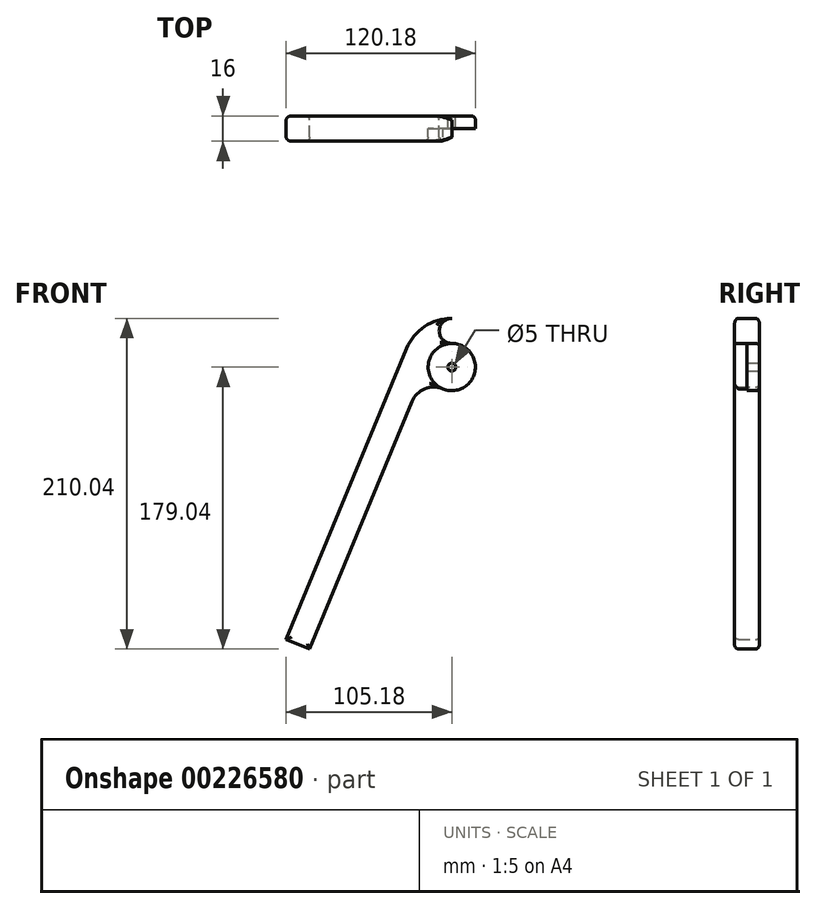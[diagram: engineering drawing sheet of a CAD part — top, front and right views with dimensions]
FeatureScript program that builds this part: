
annotation { "Feature Type Name" : "Feature", "Feature Type Description" : "" }
export const myFeature = defineFeature(function(context is Context, id is Id, definition is map)
    precondition{}
    {
        {
            var Q0;
            Q0=qCreatedBy(makeId("Front.planeOp"),FACE);
            var sketch = newSketch(context, id + "F0", { "sketchPlane" : qUnion([Q0])});
            skCircle(sketch, "E0", {"center": v(0, 0) * mm, "radius": 15 * mm});
            skCircle(sketch, "E1", {"center": v(0, 23) * mm, "radius": 8 * mm});
            skLineSegment(sketch, "E2", {"start": v(0, 0) * mm, "end": v(-46.2, 19.13) * mm});
            skArc(sketch, "E3", {"start": v(0, 31) * mm, "mid": v(-17.22, 25.78) * mm, "end": v(-28.64, 11.86) * mm});
            skLineSegment(sketch, "E4", {"start": v(-28.64, 11.86) * mm, "end": v(-105.18, -172.91) * mm});
            skLineSegment(sketch, "E5", {"start": v(-105.18, -172.91) * mm, "end": v(-90.4, -179.04) * mm});
            skLineSegment(sketch, "E6", {"start": v(-90.4, -179.04) * mm, "end": v(-13.86, 5.74) * mm});
            skLineSegment(sketch, "E7", {"start": v(0, 0) * mm, "end": v(-21.14, -51.03) * mm});
            skArc(sketch, "E8", {"start": v(-5.74, -13.86) * mm, "mid": v(-17.22, -13.86) * mm, "end": v(-25.34, -21.98) * mm});
            skSolve(sketch);
        }
        {
            var Q0;
            {var subQ3=sQuery(id+"F0.wireOp",EDGE,"E4");Q0=makeQuery(id+"F0.imprint","IMPRINT",FACE,{"disambiguationData":[TD([[makeQuery(id+"F0.imprint","IMPRINT",EDGE,{"derivedFrom":subQ3}),1.0]])]});}
            var Q1;
            {var subQ5=sQuery(id+"F0.wireOp",EDGE,"E3");Q1=makeQuery(id+"F0.imprint","IMPRINT",FACE,{"disambiguationData":[TD([[makeQuery(id+"F0.imprint","IMPRINT",EDGE,{"derivedFrom":subQ5}),1.0]])]});}
            var Q2;
            {var subQ3=sQuery(id+"F0.wireOp",EDGE,"E8");Q2=makeQuery(id+"F0.imprint","IMPRINT",FACE,{"disambiguationData":[TD([[makeQuery(id+"F0.imprint","IMPRINT",EDGE,{"derivedFrom":subQ3}),-1.0]])]});}
            extrude(context, id + "F1", {"entities" : qUnion([Q0, Q1, Q2]), "depth" : 16 * mm});
        }
        {
            var Q0;
            {var subQ0=sQuery(id+"F0.wireOp",EDGE,"E2");var subQ3=sQuery(id+"F0.wireOp",EDGE,"E7");var subQ5=makeQuery(id+"F0.imprint","INTERSECT",VERTEX,{"derivedFrom":[subQ0,subQ3]});Q0=makeQuery(id+"F0.imprint","IMPRINT",FACE,{"disambiguationData":[TD([[makeQuery(id+"F0.imprint","IMPRINT",EDGE,{"disambiguationData":[TD([[subQ5,-1.0]])],"derivedFrom":subQ0}),1.0]])]});}
            var Q1;
            {var subQ1=sQuery(id+"F0.wireOp",EDGE,"E0");var subQ3=makeQuery(id+"F0.imprint","INTERSECT",VERTEX,{"derivedFrom":[subQ1,sQuery(id+"F0.wireOp",EDGE,"E1")]});Q1=makeQuery(id+"F0.imprint","IMPRINT",FACE,{"disambiguationData":[TD([[makeQuery(id+"F0.imprint","IMPRINT",EDGE,{"disambiguationData":[TD([[subQ3,-1.0]])],"derivedFrom":subQ1}),1.0]])]});}
            extrude(context, id + "F2", {"entities" : qUnion([Q0, Q1]), "operationType" : NewBodyOperationType.ADD, "depth" : 8 * mm});
        }
        {
            var Q0;
            Q0=makeQuery(id+"F1.opExtrude","CAP_FACE",FACE,{"disambiguationData":[OSD([sQuery(id+"F0.wireOp",EDGE,"E0"),sQuery(id+"F0.wireOp",EDGE,"E1"),sQuery(id+"F0.wireOp",EDGE,"E3"),sQuery(id+"F0.wireOp",EDGE,"E4"),sQuery(id+"F0.wireOp",EDGE,"E5"),sQuery(id+"F0.wireOp",EDGE,"E6"),sQuery(id+"F0.wireOp",EDGE,"E8")])],"isStart":false});
            var Q1;
            {var subQ0=sQuery(id+"F0.wireOp",EDGE,"E0");Q1=makeQuery(id+"F2.boolean.opBoolean","MERGE",FACE,{"derivedFrom":[makeQuery(id+"F1.opExtrude","CAP_FACE",FACE,{"disambiguationData":[OSD([subQ0,sQuery(id+"F0.wireOp",EDGE,"E1"),sQuery(id+"F0.wireOp",EDGE,"E3"),sQuery(id+"F0.wireOp",EDGE,"E4"),sQuery(id+"F0.wireOp",EDGE,"E5"),sQuery(id+"F0.wireOp",EDGE,"E6"),sQuery(id+"F0.wireOp",EDGE,"E8")])],"isStart":true}),makeQuery(id+"F2.opExtrude","CAP_FACE",FACE,{"disambiguationData":[OSD([subQ0])],"isStart":true})]});}
            fillet(context, id + "F3", {"entities" : qUnion([Q0, Q1]), "radius" : 2.5 * mm, "tangentPropagation" : true, "allowEdgeOverflow" : false});
        }
        {
            var Q0;
            Q0=sQuery(id+"F0.wireOp",VERTEX,"E7.start");
            var Q1;
            Q1=makeQuery(id+"F1.opExtrude","SWEPT_BODY",BODY,{"disambiguationData":[OSD([sQuery(id+"F0.wireOp",EDGE,"E0"),sQuery(id+"F0.wireOp",EDGE,"E1"),sQuery(id+"F0.wireOp",EDGE,"E3"),sQuery(id+"F0.wireOp",EDGE,"E4"),sQuery(id+"F0.wireOp",EDGE,"E5"),sQuery(id+"F0.wireOp",EDGE,"E6"),sQuery(id+"F0.wireOp",EDGE,"E8")])]});
            hole(context, id + "F4", {"style" : HoleStyle.SIMPLE, "endStyle" : HoleEndStyle.THROUGH, "oppositeDirection" : true, "holeDiameter" : 5 * mm, "locations" : qUnion([Q0]), "scope" : qUnion([Q1]), "isTappedThrough" : true});
        }
    });
